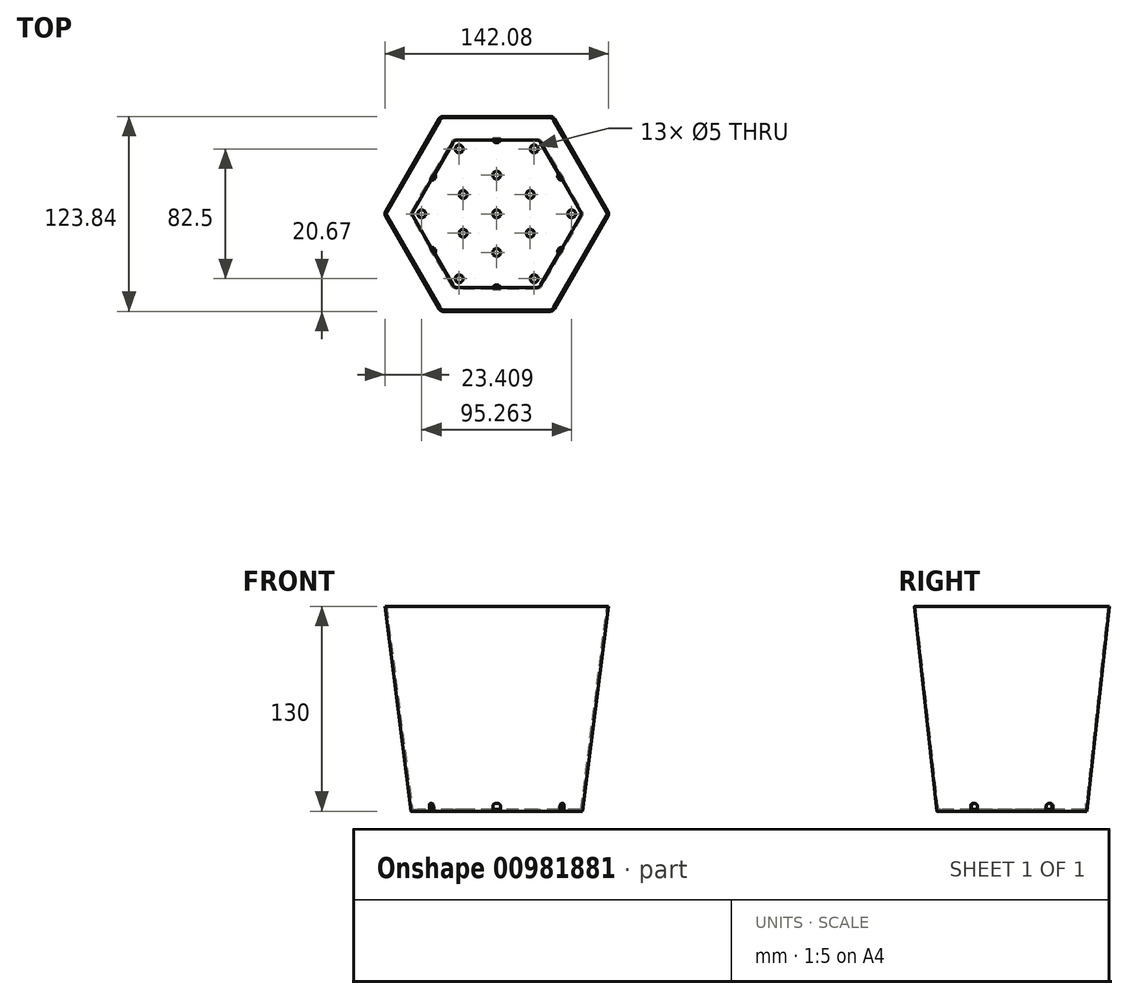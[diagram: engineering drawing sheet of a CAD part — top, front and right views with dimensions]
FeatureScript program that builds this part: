
annotation { "Feature Type Name" : "Feature", "Feature Type Description" : "" }
export const myFeature = defineFeature(function(context is Context, id is Id, definition is map)
    precondition{}
    {
        {
            var Q0;
            Q0=qCreatedBy(makeId("Top.planeOp"),FACE);
            var sketch = newSketch(context, id + "F0", { "sketchPlane" : qUnion([Q0])});
            skLineSegment(sketch, "E0", {"start": v(0, 0) * mm, "end": v(55, 0) * mm});
            skCircle(sketch, "E1.cCircle", {"center": v(0, 0) * mm, "radius": 55 * mm, "construction": true});
            skLineSegment(sketch, "E1.0", {"start": v(55, 0) * mm, "end": v(27.5, -47.63) * mm});
            skLineSegment(sketch, "E1.1", {"start": v(27.5, -47.63) * mm, "end": v(-27.5, -47.63) * mm});
            skLineSegment(sketch, "E1.2", {"start": v(-27.5, -47.63) * mm, "end": v(-55, 0) * mm});
            skLineSegment(sketch, "E1.3", {"start": v(-55, 0) * mm, "end": v(-27.5, 47.63) * mm});
            skLineSegment(sketch, "E1.4", {"start": v(-27.5, 47.63) * mm, "end": v(27.5, 47.63) * mm});
            skLineSegment(sketch, "E1.5", {"start": v(27.5, 47.63) * mm, "end": v(55, 0) * mm});
            skSolve(sketch);
        }
        {
            var Q0;
            Q0=qCreatedBy(makeId("Front.planeOp"),FACE);
            var sketch = newSketch(context, id + "F1", { "sketchPlane" : qUnion([Q0])});
            skLineSegment(sketch, "E2", {"start": v(0, 0) * mm, "end": v(0, 1) * mm});
            skLineSegment(sketch, "E3", {"start": v(0, 1) * mm, "end": v(54, 1) * mm});
            skLineSegment(sketch, "E4", {"start": v(0, 0) * mm, "end": v(0, 130) * mm, "construction": true});
            skLineSegment(sketch, "E5", {"start": v(0, 130) * mm, "end": v(71.5, 130) * mm});
            skLineSegment(sketch, "E6.0", {"start": v(0, 0) * mm, "end": v(55, 0) * mm});
            skLineSegment(sketch, "E7", {"start": v(55, 0) * mm, "end": v(71.5, 130) * mm});
            skLineSegment(sketch, "E8", {"start": v(71.5, 130) * mm, "end": v(70.5, 130) * mm});
            skLineSegment(sketch, "E9", {"start": v(70.5, 130) * mm, "end": v(54, 1) * mm});
            skSolve(sketch);
        }
        {
            var Q0;
            Q0=makeQuery(id+"F1.imprint","IMPRINT",FACE,{"disambiguationData":[TD([[makeQuery(id+"F1.imprint","IMPRINT",EDGE,{"derivedFrom":sQuery(id+"F1.wireOp",EDGE,"E2")}),-1.0]])]});
            var Q1;
            Q1=sQuery(id+"F0.wireOp",EDGE,"E1.0");
            var Q2;
            Q2=sQuery(id+"F0.wireOp",EDGE,"E1.1");
            var Q3;
            Q3=sQuery(id+"F0.wireOp",EDGE,"E1.2");
            var Q4;
            Q4=sQuery(id+"F0.wireOp",EDGE,"E1.3");
            var Q5;
            Q5=sQuery(id+"F0.wireOp",EDGE,"E1.4");
            var Q6;
            Q6=sQuery(id+"F0.wireOp",EDGE,"E1.5");
            sweep(context, id + "F2", {"profiles" : qUnion([Q0]), "path" : qUnion([Q1, Q2, Q3, Q4, Q5, Q6])});
        }
        {
            var Q0;
            Q0=makeQuery(id+"F2.opSweep","SWEPT_FACE",FACE,{"disambiguationData":[OSD([sQuery(id+"F0.wireOp",EDGE,"E1.0"),sQuery(id+"F1.wireOp",EDGE,"E6.0")])]});
            var sketch = newSketch(context, id + "F3", { "sketchPlane" : qUnion([Q0])});
            skCircle(sketch, "E10", {"center": v(0, 47.63) * mm, "radius": 2.5 * mm});
            skCircle(sketch, "E11.1.0", {"center": v(-23.82, 41.25) * mm, "radius": 2.5 * mm});
            skCircle(sketch, "E11.2.0", {"center": v(-41.25, 23.82) * mm, "radius": 2.5 * mm});
            skCircle(sketch, "E11.3.0", {"center": v(-47.63, 0) * mm, "radius": 2.5 * mm});
            skCircle(sketch, "E11.4.0", {"center": v(-41.25, -23.82) * mm, "radius": 2.5 * mm});
            skCircle(sketch, "E11.5.0", {"center": v(-23.82, -41.25) * mm, "radius": 2.5 * mm});
            skPoint(sketch, "E11.center", {"position": v(0, 0) * mm});
            skCircle(sketch, "E12", {"center": v(0, 24.6) * mm, "radius": 2.5 * mm});
            skCircle(sketch, "E13.1.0", {"center": v(-21.3, 12.3) * mm, "radius": 2.5 * mm});
            skCircle(sketch, "E13.2.0", {"center": v(-21.3, -12.3) * mm, "radius": 2.5 * mm});
            skCircle(sketch, "E13.3.0", {"center": v(0, -24.6) * mm, "radius": 2.5 * mm});
            skCircle(sketch, "E13.4.0", {"center": v(21.3, -12.3) * mm, "radius": 2.5 * mm});
            skCircle(sketch, "E13.5.0", {"center": v(21.3, 12.3) * mm, "radius": 2.5 * mm});
            skCircle(sketch, "E14", {"center": v(0, 0) * mm, "radius": 2.5 * mm});
            skCircle(sketch, "E15.1.6.0", {"center": v(0, -47.63) * mm, "radius": 2.5 * mm});
            skCircle(sketch, "E15.1.7.0", {"center": v(23.82, -41.25) * mm, "radius": 2.5 * mm});
            skCircle(sketch, "E15.1.8.0", {"center": v(41.25, -23.82) * mm, "radius": 2.5 * mm});
            skCircle(sketch, "E15.1.9.0", {"center": v(47.63, 0) * mm, "radius": 2.5 * mm});
            skCircle(sketch, "E15.1.10.0", {"center": v(41.25, 23.82) * mm, "radius": 2.5 * mm});
            skCircle(sketch, "E15.1.11.0", {"center": v(23.82, 41.25) * mm, "radius": 2.5 * mm});
            skSolve(sketch);
        }
        {
            var Q0;
            Q0 = qSketchRegion(id + "F3", true);
            extrude(context, id + "F4", {"entities" : qUnion([Q0]), "operationType" : NewBodyOperationType.REMOVE, "oppositeDirection" : true, "depth" : 5 * mm, "offsetDistance" : 25 * mm});
        }
        {
            var Q0;
            Q0=makeQuery(id+"F4.boolean.opBoolean","COPY",EDGE,{"disambiguationData":[OD(1.0)],"derivedFrom":makeQuery(id+"F4.opExtrude","CAP_EDGE",EDGE,{"disambiguationData":[OSD([sQuery(id+"F3.wireOp",EDGE,"E15.1.6.0")])],"isStart":false})});
            var Q1;
            Q1=makeQuery(id+"F4.boolean.opBoolean","COPY",EDGE,{"disambiguationData":[OD(0.0)],"derivedFrom":makeQuery(id+"F4.opExtrude","CAP_EDGE",EDGE,{"disambiguationData":[OSD([sQuery(id+"F3.wireOp",EDGE,"E15.1.6.0")])],"isStart":false})});
            var Q2;
            Q2=makeQuery(id+"F4.boolean.opBoolean","COPY",EDGE,{"disambiguationData":[OD(0.0)],"derivedFrom":makeQuery(id+"F4.opExtrude","CAP_EDGE",EDGE,{"disambiguationData":[OSD([sQuery(id+"F3.wireOp",EDGE,"E15.1.8.0")])],"isStart":false})});
            var Q3;
            Q3=makeQuery(id+"F4.boolean.opBoolean","COPY",EDGE,{"disambiguationData":[OD(0.0)],"derivedFrom":makeQuery(id+"F4.opExtrude","CAP_EDGE",EDGE,{"disambiguationData":[OSD([sQuery(id+"F3.wireOp",EDGE,"E15.1.10.0")])],"isStart":false})});
            var Q4;
            Q4=makeQuery(id+"F4.boolean.opBoolean","COPY",EDGE,{"disambiguationData":[OD(1.0)],"derivedFrom":makeQuery(id+"F4.opExtrude","CAP_EDGE",EDGE,{"disambiguationData":[OSD([sQuery(id+"F3.wireOp",EDGE,"E10")])],"isStart":false})});
            var Q5;
            Q5=makeQuery(id+"F4.boolean.opBoolean","COPY",EDGE,{"disambiguationData":[OD(1.0)],"derivedFrom":makeQuery(id+"F4.opExtrude","CAP_EDGE",EDGE,{"disambiguationData":[OSD([sQuery(id+"F3.wireOp",EDGE,"E11.2.0")])],"isStart":false})});
            var Q6;
            Q6=makeQuery(id+"F4.boolean.opBoolean","COPY",EDGE,{"disambiguationData":[OD(1.0)],"derivedFrom":makeQuery(id+"F4.opExtrude","CAP_EDGE",EDGE,{"disambiguationData":[OSD([sQuery(id+"F3.wireOp",EDGE,"E11.4.0")])],"isStart":false})});
            fillet(context, id + "F5", {"entities" : qUnion([Q0, Q1, Q2, Q3, Q4, Q5, Q6]), "tangentPropagation" : true, "radius" : 2 * mm, "defaultsChanged" : false, "vertexSettings" : [], "allowEdgeOverflow" : false});
        }
        {
            var Q0;
            Q0=makeQuery(id+"F2.opSweep","MID_CAP_EDGE",EDGE,{"disambiguationData":[OSD([sQuery(id+"F0.wireOp",VERTEX,"E1.5.start"),sQuery(id+"F1.wireOp",EDGE,"E7")])],"capPos":5.0});
            var Q1;
            Q1=makeQuery(id+"F2.opSweep","MID_CAP_EDGE",EDGE,{"disambiguationData":[OSD([sQuery(id+"F0.wireOp",VERTEX,"E1.4.start"),sQuery(id+"F1.wireOp",EDGE,"E7")])],"capPos":4.0});
            var Q2;
            Q2=makeQuery(id+"F2.opSweep","CAP_EDGE",EDGE,{"disambiguationData":[OSD([sQuery(id+"F0.wireOp",VERTEX,"E1.5.end"),sQuery(id+"F1.wireOp",EDGE,"E9")])],"isStart":true});
            var Q3;
            Q3=makeQuery(id+"F2.opSweep","MID_CAP_EDGE",EDGE,{"disambiguationData":[OSD([sQuery(id+"F0.wireOp",VERTEX,"E1.1.start"),sQuery(id+"F1.wireOp",EDGE,"E9")])],"capPos":1.0});
            var Q4;
            Q4=makeQuery(id+"F2.opSweep","MID_CAP_EDGE",EDGE,{"disambiguationData":[OSD([sQuery(id+"F0.wireOp",VERTEX,"E1.5.start"),sQuery(id+"F1.wireOp",EDGE,"E9")])],"capPos":5.0});
            var Q5;
            Q5=makeQuery(id+"F2.opSweep","MID_CAP_EDGE",EDGE,{"disambiguationData":[OSD([sQuery(id+"F0.wireOp",VERTEX,"E1.3.start"),sQuery(id+"F1.wireOp",EDGE,"E7")])],"capPos":3.0});
            var Q6;
            Q6=makeQuery(id+"F2.opSweep","MID_CAP_EDGE",EDGE,{"disambiguationData":[OSD([sQuery(id+"F0.wireOp",VERTEX,"E1.2.start"),sQuery(id+"F1.wireOp",EDGE,"E7")])],"capPos":2.0});
            var Q7;
            Q7=makeQuery(id+"F2.opSweep","MID_CAP_EDGE",EDGE,{"disambiguationData":[OSD([sQuery(id+"F0.wireOp",VERTEX,"E1.1.start"),sQuery(id+"F1.wireOp",EDGE,"E7")])],"capPos":1.0});
            var Q8;
            Q8=makeQuery(id+"F2.opSweep","MID_CAP_EDGE",EDGE,{"disambiguationData":[OSD([sQuery(id+"F0.wireOp",VERTEX,"E1.4.start"),sQuery(id+"F1.wireOp",EDGE,"E9")])],"capPos":4.0});
            var Q9;
            Q9=makeQuery(id+"F2.opSweep","MID_CAP_EDGE",EDGE,{"disambiguationData":[OSD([sQuery(id+"F0.wireOp",VERTEX,"E1.3.start"),sQuery(id+"F1.wireOp",EDGE,"E9")])],"capPos":3.0});
            var Q10;
            Q10=makeQuery(id+"F2.opSweep","MID_CAP_EDGE",EDGE,{"disambiguationData":[OSD([sQuery(id+"F0.wireOp",VERTEX,"E1.2.start"),sQuery(id+"F1.wireOp",EDGE,"E9")])],"capPos":2.0});
            var Q11;
            Q11=makeQuery(id+"F2.opSweep","CAP_EDGE",EDGE,{"disambiguationData":[OSD([sQuery(id+"F0.wireOp",VERTEX,"E1.5.end"),sQuery(id+"F1.wireOp",EDGE,"E7")])],"isStart":true});
            fillet(context, id + "F6", {"entities" : qUnion([Q0, Q1, Q2, Q3, Q4, Q5, Q6, Q7, Q8, Q9, Q10, Q11]), "tangentPropagation" : true, "radius" : 3 * mm, "defaultsChanged" : true, "vertexSettings" : [], "allowEdgeOverflow" : false});
        }
    });
